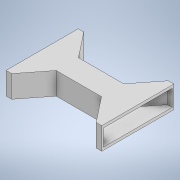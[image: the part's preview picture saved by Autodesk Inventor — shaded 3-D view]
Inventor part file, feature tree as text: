
AUTODESK INVENTOR PART (.ipt)
format: ipt  version: 2022 (Build 260153000, 153)  size: 166,400 bytes
history: native  units: mm
features: extrude x3, sketch x3
ambient origin geometry x8: Origin, YZ Plane, XZ Plane, XY Plane, X Axis, Y Axis, Z Axis, Center Point
bodies: Solid1 (feature_tree)
feature tree (6):
  extrude  "Extrusion1"  Depth=65.0mm
  extrude  "Extrusion2"  Depth=65.0mm
  extrude  "Extrusion3"  Depth=3.0mm
  sketch  "Sketch1"  dims[d0=172.412mm d1=65.0mm]
  sketch  "Sketch2"  dims[d2=65.0mm d7=10.0mm]
  sketch  "Sketch3"  dims[d8=5.0mm d9=0.0mm d10=3.0mm d11=30.0mm d12=0.0mm d13=5.0mm d14=0.0mm]
